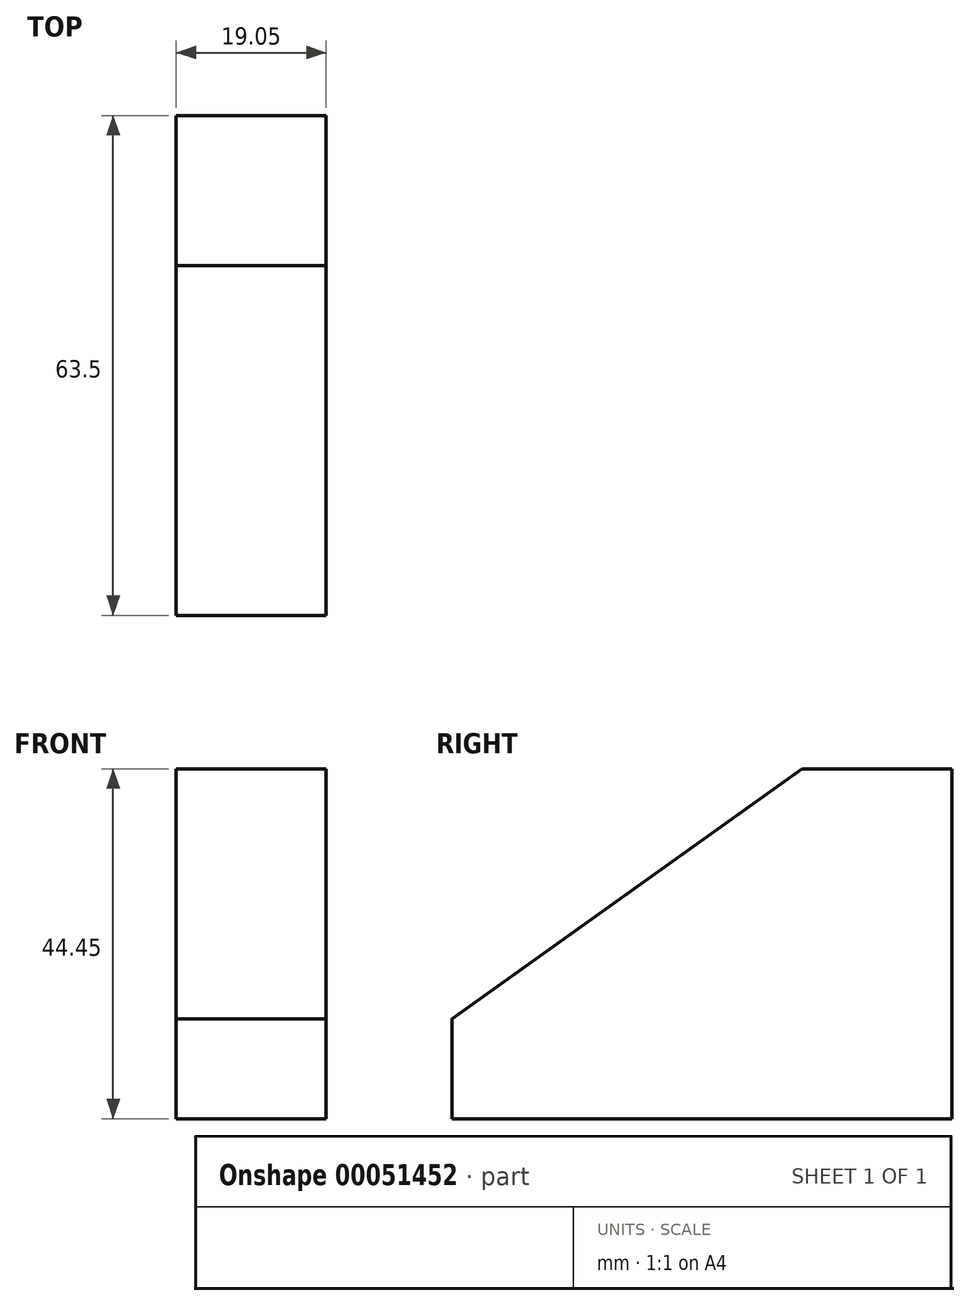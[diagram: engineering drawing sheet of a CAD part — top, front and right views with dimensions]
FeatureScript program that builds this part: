
annotation { "Feature Type Name" : "Feature", "Feature Type Description" : "" }
export const myFeature = defineFeature(function(context is Context, id is Id, definition is map)
    precondition{}
    {
        {
            var Q0;
            Q0=qCreatedBy(makeId("Right.planeOp"),FACE);
            var sketch = newSketch(context, id + "F0", { "sketchPlane" : qUnion([Q0])});
            skLineSegment(sketch, "E0", {"start": v(18.2, 12.95) * mm, "end": v(18.2, -31.5) * mm});
            skLineSegment(sketch, "E1", {"start": v(18.2, -31.5) * mm, "end": v(-45.3, -31.5) * mm});
            skLineSegment(sketch, "E2", {"start": v(-45.3, -31.5) * mm, "end": v(-45.3, -18.8) * mm});
            skLineSegment(sketch, "E3", {"start": v(18.2, 12.95) * mm, "end": v(-0.84, 12.95) * mm});
            skLineSegment(sketch, "E4", {"start": v(-0.84, 12.95) * mm, "end": v(-45.3, -18.8) * mm});
            skSolve(sketch);
        }
        {
            var Q0;
            Q0=makeQuery(id+"F0.imprint","IMPRINT",FACE,{"disambiguationData":[TD([[makeQuery(id+"F0.imprint","IMPRINT",EDGE,{"derivedFrom":sQuery(id+"F0.wireOp",EDGE,"E0")}),-1.0]])]});
            extrude(context, id + "F1", {"entities" : qUnion([Q0]), "depth" : 19.05 * mm});
        }
    });
